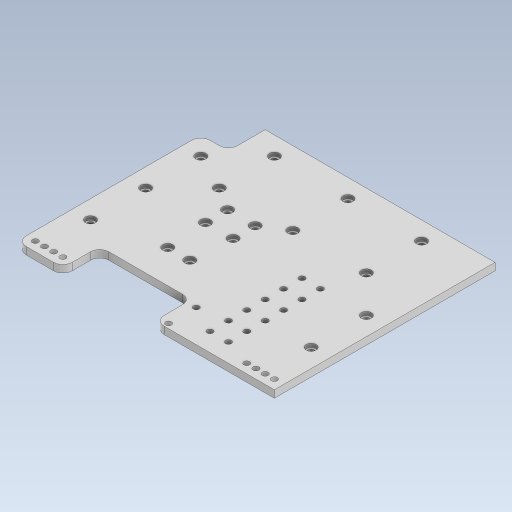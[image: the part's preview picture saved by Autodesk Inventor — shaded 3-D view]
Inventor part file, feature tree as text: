
AUTODESK INVENTOR PART (.ipt)
format: ipt  version: 2023.5 (Build 275446000, 446)  size: 542,720 bytes
history: native  units: in
note: dims shown in document units (in); Inventor stores cm internally (conversion verified against a paired STEP export)
features: extrude x2, sketch x1, fillet x1
ambient origin geometry x8: Origin, YZ Plane, XZ Plane, XY Plane, X Axis, Y Axis, Z Axis, Center Point
bodies: Solid1 (feature_tree)
feature tree (4):
  sketch  "Sketch1"  dims[d0=5.5118in d1=4.7244in d2=1.9685in d3=0.7874in d4=0.9843in d5=0.126in d6=0.1969in d7=0.1969in d8=0.126in d9=0.1969in d10=0.126in d11=0.1969in d12=0.126in d13=0.1969in d14=0.126in d15=0.3937in d16=1.1811in d17=0.126in d18=0.2165in d19=0.2165in d20=0.126in d22=0.2165in d23=0.126in d24=0.2165in d28=0.126in d30=0.2165in d34=0.126in d37=0.2165in d38=0.1575in d39=0.0in d40=0.0787in d41=0.0in d42=1.1811in d43=0.3937in d44=0.3937in d46=0.3937in d47=0.126in d48=0.1969in d49=0.0984in d50=0.126in d51=0.5906in d52=0.126in d53=0.126in d54=0.3937in d55=0.126in d56=0.3937in d57=0.126in d58=0.7874in d59=0.3937in d60=0.3937in d61=0.126in d62=0.3937in d63=0.126in d64=0.3937in d65=0.126in d66=0.126in d67=0.126in d68=0.3937in d69=0.126in d70=0.3937in d71=0.126in d72=0.126in d73=0.1299in d74=0.2165in d76=0.1299in d77=0.2165in d78=1.1811in d79=1.1811in d80=0.5906in d81=0.7874in d82=0.1969in]
  extrude  "Extrusion1"  Depth=4.7244in
  extrude  "Extrusion2"  Depth=1.9685in
  fillet  "Fillet1"  Radius=0.7874in
